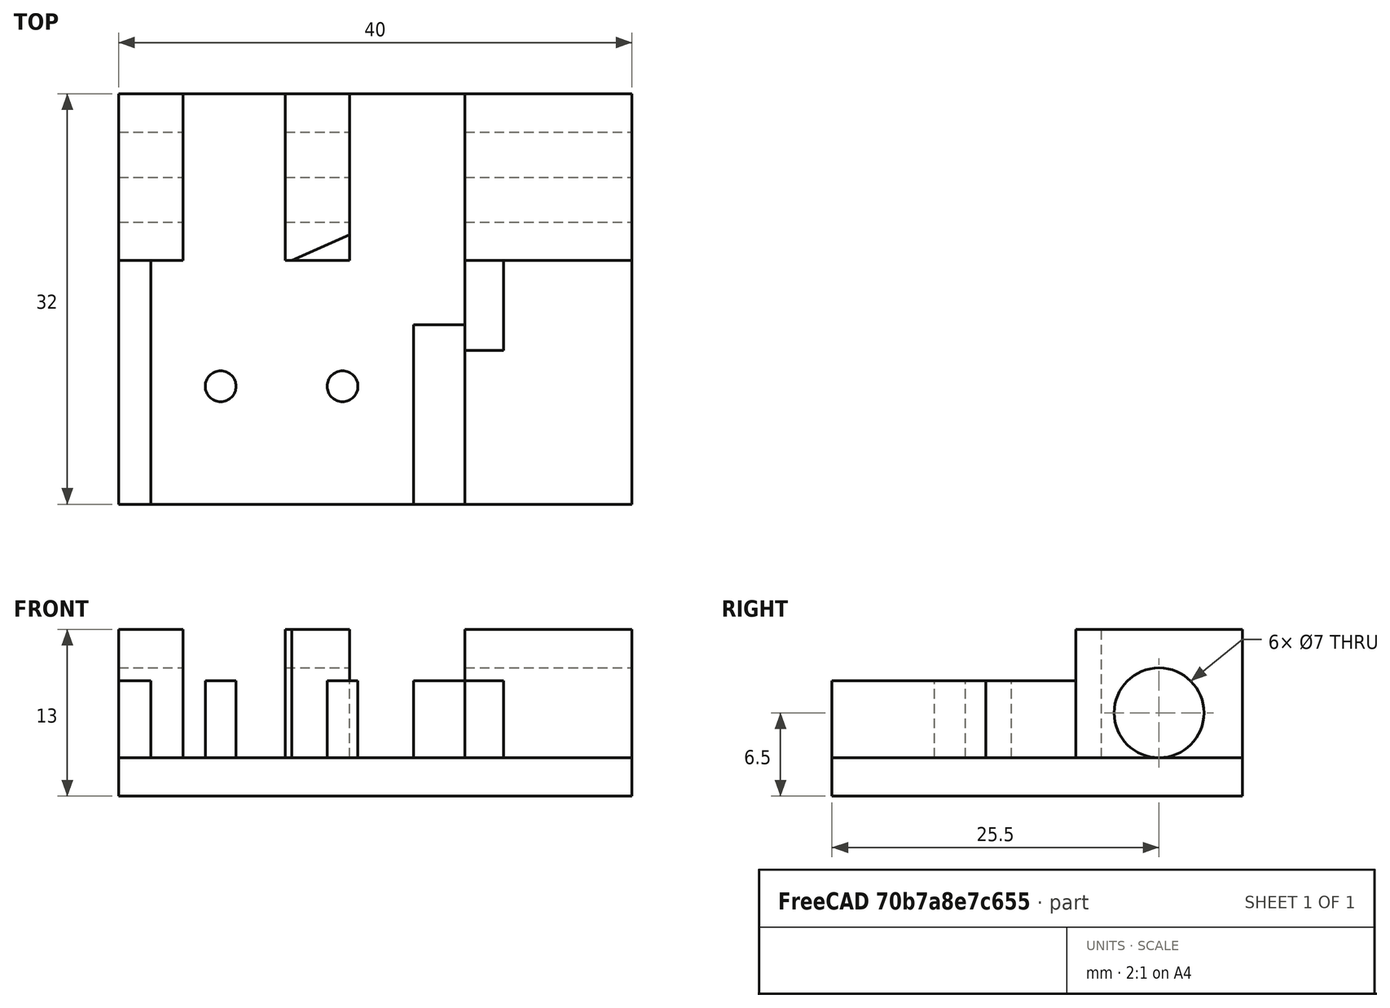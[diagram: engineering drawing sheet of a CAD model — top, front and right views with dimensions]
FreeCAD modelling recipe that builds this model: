
FCSTD DOCUMENT  (FreeCAD 0.19R)
Label: PowerPinFrame
License: All rights reserved
LicenseURL: http://en.wikipedia.org/wiki/All_rights_reserved
objects: Part::Box×7, Part::Cylinder×3, Part::MultiFuse×3, Part::Cut×2, Part::Chamfer×1
note: 16 computed .brp shape members not serialized (recipe doc carries the construction recipe); baked Part::Feature solids carry a one-line shape summary decoded from their .brp

FEATURE [Part::Box] Box  label="Base Plate"
  AttacherType = Attacher::AttachEngine3D
  Height = 3
  Length = 40
  Width = 32
FEATURE [Part::Box] Box001  label="Pin Block 1"
  AttacherType = Attacher::AttachEngine3D
  Height = 10
  Length = 5
  Placement = pos=(0,19,3) rot=(0,0,1;0rad)
  Width = 13
FEATURE [Part::Box] Box003  label="Pin Block 3"
  AttacherType = Attacher::AttachEngine3D
  Height = 10
  Length = 13
  Placement = pos=(27,19,3) rot=(0,0,1;0rad)
  Width = 13
FEATURE [Part::Box] Box004  label="Switch wall right"
  AttacherType = Attacher::AttachEngine3D
  Height = 6
  Length = 4
  Placement = pos=(23,0,3) rot=(0,0,1;0rad)
  Width = 14
FEATURE [Part::Box] Box005  label="Switch wall left"
  AttacherType = Attacher::AttachEngine3D
  Height = 6
  Length = 2.5
  Placement = pos=(0,0,3) rot=(0,0,1;0rad)
  Width = 19
FEATURE [Part::Cylinder] Cylinder001
  Angle = 360
  AttacherType = Attacher::AttachEngine3D
  Height = 6
  Placement = pos=(7.95,2.5,0) rot=(0,0,1;0rad)
  Radius = 1.2
FEATURE [Part::Cylinder] Cylinder002
  Angle = 360
  AttacherType = Attacher::AttachEngine3D
  Height = 6
  Placement = pos=(17.45,2.5,0) rot=(0,0,1;0rad)
  Radius = 1.2
FEATURE [Part::MultiFuse] Fusion  label="Switch Pins"
  Placement = pos=(0,6.7,3) rot=(0,0,1;0rad)
  Shapes = -> [Cylinder001,Cylinder002]
FEATURE [Part::Cylinder] Cylinder  label="Locking Pin Model"
  Angle = 360
  AttacherType = Attacher::AttachEngine3D
  Height = 40
  Placement = pos=(0,25.5,6.5) rot=(0,1,0;1.5708rad)
  Radius = 3.5
FEATURE [Part::Box] Box006  label="Dust cover block"
  AttacherType = Attacher::AttachEngine3D
  Height = 6
  Length = 3
  Placement = pos=(27,12,3) rot=(0,0,1;0rad)
  Width = 7
FEATURE [Part::Box] Box002  label="Pin Block 2"
  AttacherType = Attacher::AttachEngine3D
  Height = 10
  Length = 5
  Placement = pos=(13,19,3) rot=(0,0,1;0rad)
  Width = 13
FEATURE [Part::MultiFuse] Fusion001  label="Pin Blocks Base"
  Shapes = -> [Box001,Box002,Box003]
FEATURE [Part::Cut] Cut  label="Pin Blocks Holed - deprecated"
  Base = -> Fusion001
  Tool = -> Cylinder
FEATURE [Part::Chamfer] Chamfer  label="Pin Block 2 - with arm cut"
  Base = -> Box002
  Edges = 1 edges: [Edge5 r1=2 r2=4.5]
FEATURE [Part::MultiFuse] Fusion002
  Shapes = -> [Chamfer,Box001,Box003]
FEATURE [Part::Cut] Cut001  label="Pin Blocks Holed"
  Base = -> Fusion002
  Tool = -> Cylinder
